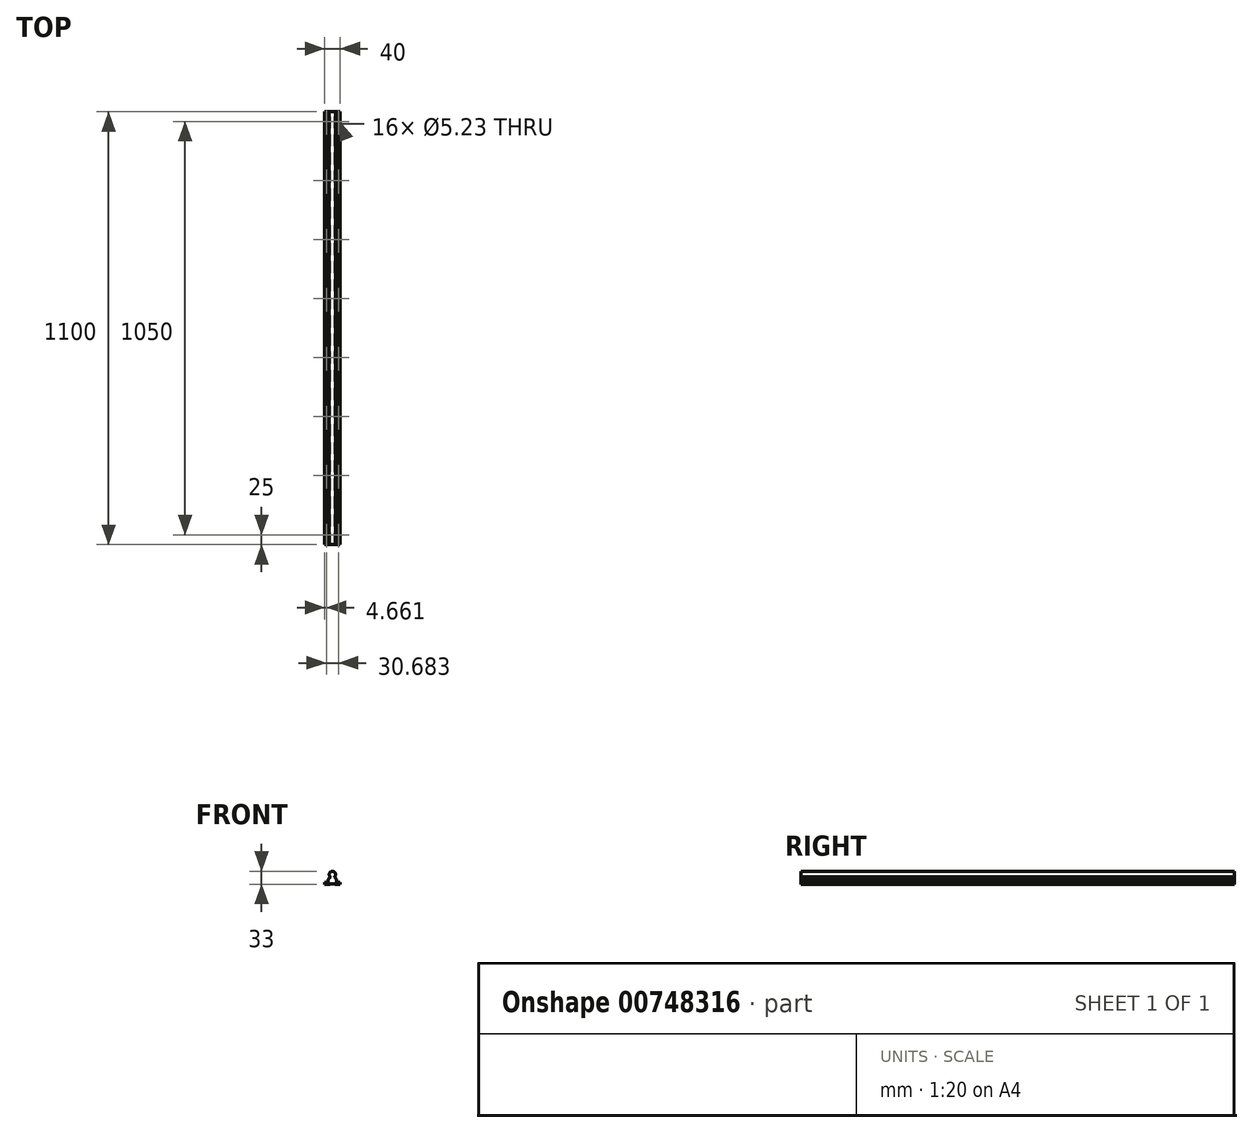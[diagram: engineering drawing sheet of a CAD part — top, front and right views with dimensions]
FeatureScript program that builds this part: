
annotation { "Feature Type Name" : "Feature", "Feature Type Description" : "" }
export const myFeature = defineFeature(function(context is Context, id is Id, definition is map)
    precondition{}
    {
        {
            var Q0;
            Q0=qCreatedBy(makeId("Front.planeOp"),FACE);
            var sketch = newSketch(context, id + "F0", { "sketchPlane" : qUnion([Q0])});
            skCircle(sketch, "E0", {"center": v(0, 0) * mm, "radius": 8 * mm});
            skLineSegment(sketch, "E1", {"start": v(0, 10.3) * mm, "end": v(0, -10.85) * mm, "construction": true});
            skLineSegment(sketch, "E2", {"start": v(12.1, 0) * mm, "end": v(-10.9, 0) * mm, "construction": true});
            skLineSegment(sketch, "E3", {"start": v(-5, -6.24) * mm, "end": v(-10.67, -13) * mm});
            skLineSegment(sketch, "E4", {"start": v(-10.67, -13) * mm, "end": v(-10.67, -20) * mm});
            skLineSegment(sketch, "E5", {"start": v(-10.67, -20) * mm, "end": v(-20, -20) * mm});
            skLineSegment(sketch, "E6", {"start": v(-20, -20) * mm, "end": v(-20, -25) * mm});
            skLineSegment(sketch, "E7", {"start": v(-20, -25) * mm, "end": v(20, -25) * mm});
            skLineSegment(sketch, "E8", {"start": v(20, -25) * mm, "end": v(20, -20) * mm});
            skLineSegment(sketch, "E9", {"start": v(20, -20) * mm, "end": v(16.54, -20) * mm});
            skLineSegment(sketch, "E10", {"start": v(10.67, -13) * mm, "end": v(5, -6.24) * mm});
            skLineSegment(sketch, "E11", {"start": v(10.67, -13) * mm, "end": v(10.67, -20) * mm});
            skLineSegment(sketch, "E12", {"start": v(10.67, -20) * mm, "end": v(16.54, -20) * mm});
            skSolve(sketch);
        }
        {
            var Q0;
            Q0 = qSketchRegion(id + "F0", true);
            extrude(context, id + "F1", {"entities" : qUnion([Q0]), "depth" : 1100 * mm, "offsetDistance" : 25.4 * mm});
        }
        {
            var Q0;
            Q0=makeQuery(id+"F1.opExtrude","SWEPT_FACE",FACE,{"disambiguationData":[OSD([sQuery(id+"F0.wireOp",EDGE,"E7")])]});
            var sketch = newSketch(context, id + "F2", { "sketchPlane" : qUnion([Q0])});
            skLineSegment(sketch, "E13", {"start": v(0, 1100) * mm, "end": v(0, 0) * mm, "construction": true});
            skLineSegment(sketch, "E14.0", {"start": v(-6.35, 1150) * mm, "end": v(-6.35, 0) * mm, "construction": true});
            skLineSegment(sketch, "E15.0", {"start": v(6.35, 1150) * mm, "end": v(6.35, 0) * mm, "construction": true});
            skLineSegment(sketch, "E16.bottom", {"start": v(-6.35, 1150) * mm, "end": v(6.35, 1150) * mm});
            skLineSegment(sketch, "E16.top", {"start": v(-6.35, 0) * mm, "end": v(6.35, 0) * mm});
            skLineSegment(sketch, "E16.left", {"start": v(-6.35, 1150) * mm, "end": v(-6.35, 0) * mm});
            skLineSegment(sketch, "E16.right", {"start": v(6.35, 1150) * mm, "end": v(6.35, 0) * mm});
            skSolve(sketch);
        }
        {
            var Q0;
            Q0 = qSketchRegion(id + "F2", true);
            extrude(context, id + "F3", {"entities" : qUnion([Q0]), "operationType" : NewBodyOperationType.REMOVE, "oppositeDirection" : true, "depth" : 1.59 * mm, "offsetDistance" : 25.4 * mm});
        }
        {
            var Q0;
            {var subQ5=sQuery(id+"F0.wireOp",EDGE,"E7");var subQ6=sQuery(id+"F0.wireOp",EDGE,"E6");Q0=makeQuery(id+"F3.boolean.opBoolean","SPLIT",FACE,{"disambiguationData":[TD([makeQuery(id+"F1.opExtrude","SWEPT_FACE",FACE,{"disambiguationData":[OSD([subQ6])]})])],"derivedFrom":makeQuery(id+"F1.opExtrude","SWEPT_FACE",FACE,{"disambiguationData":[OSD([subQ5])]})});}
            var sketch = newSketch(context, id + "F4", { "sketchPlane" : qUnion([Q0])});
            skLineSegment(sketch, "E17", {"start": v(-20, 550) * mm, "end": v(-6.35, 550) * mm, "construction": true});
            skLineSegment(sketch, "E18", {"start": v(-15.34, 550) * mm, "end": v(15.34, 550) * mm, "construction": true});
            skLineSegment(sketch, "E19.0", {"start": v(-15.34, 475) * mm, "end": v(15.34, 475) * mm, "construction": true});
            skLineSegment(sketch, "E20.0", {"start": v(-15.34, 325) * mm, "end": v(15.34, 325) * mm, "construction": true});
            skLineSegment(sketch, "E21.0", {"start": v(-15.34, 175) * mm, "end": v(15.34, 175) * mm, "construction": true});
            skLineSegment(sketch, "E22.0", {"start": v(-15.34, 25) * mm, "end": v(15.34, 25) * mm, "construction": true});
            skLineSegment(sketch, "E23.0", {"start": v(-15.34, 625) * mm, "end": v(15.34, 625) * mm, "construction": true});
            skLineSegment(sketch, "E24.0", {"start": v(-15.34, 775) * mm, "end": v(15.34, 775) * mm, "construction": true});
            skLineSegment(sketch, "E25.0", {"start": v(-15.34, 925) * mm, "end": v(15.34, 925) * mm, "construction": true});
            skLineSegment(sketch, "E26.0", {"start": v(-15.34, 1075) * mm, "end": v(15.34, 1075) * mm, "construction": true});
            skCircle(sketch, "E27", {"center": v(-15.34, 1075) * mm, "radius": 2.62 * mm});
            skCircle(sketch, "E28", {"center": v(15.34, 1075) * mm, "radius": 2.62 * mm});
            skCircle(sketch, "E29", {"center": v(-15.34, 925) * mm, "radius": 2.62 * mm});
            skCircle(sketch, "E30", {"center": v(15.34, 925) * mm, "radius": 2.62 * mm});
            skCircle(sketch, "E31", {"center": v(-15.34, 775) * mm, "radius": 2.62 * mm});
            skCircle(sketch, "E32", {"center": v(15.34, 775) * mm, "radius": 2.62 * mm});
            skCircle(sketch, "E33", {"center": v(-15.34, 625) * mm, "radius": 2.62 * mm});
            skCircle(sketch, "E34", {"center": v(15.34, 625) * mm, "radius": 2.62 * mm});
            skCircle(sketch, "E35", {"center": v(-15.34, 475) * mm, "radius": 2.62 * mm});
            skCircle(sketch, "E36", {"center": v(15.34, 475) * mm, "radius": 2.62 * mm});
            skCircle(sketch, "E37", {"center": v(-15.34, 325) * mm, "radius": 2.62 * mm});
            skCircle(sketch, "E38", {"center": v(15.34, 325) * mm, "radius": 2.62 * mm});
            skCircle(sketch, "E39", {"center": v(-15.34, 175) * mm, "radius": 2.62 * mm});
            skCircle(sketch, "E40", {"center": v(15.34, 175) * mm, "radius": 2.62 * mm});
            skCircle(sketch, "E41", {"center": v(-15.34, 25) * mm, "radius": 2.62 * mm});
            skCircle(sketch, "E42", {"center": v(15.34, 25) * mm, "radius": 2.62 * mm});
            skSolve(sketch);
        }
        {
            var Q0;
            Q0 = qSketchRegion(id + "F4", true);
            extrude(context, id + "F5", {"entities" : qUnion([Q0]), "operationType" : NewBodyOperationType.REMOVE, "endBound" : BoundingType.THROUGH_ALL, "oppositeDirection" : true, "depth" : 25.4 * mm, "offsetDistance" : 25.4 * mm});
        }
    });
